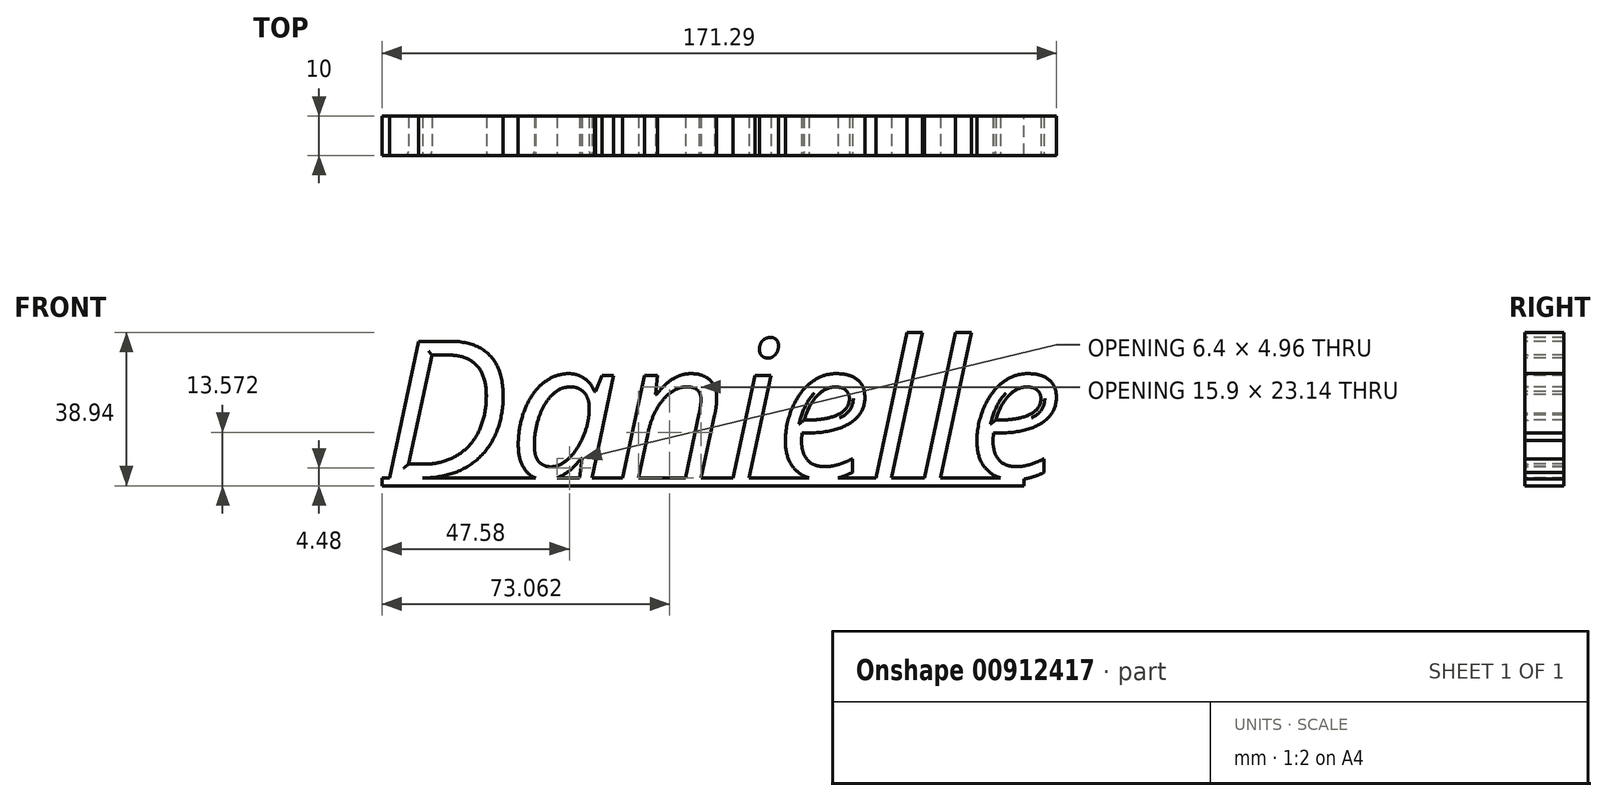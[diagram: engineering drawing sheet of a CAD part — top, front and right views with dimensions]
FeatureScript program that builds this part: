
annotation { "Feature Type Name" : "Feature", "Feature Type Description" : "" }
export const myFeature = defineFeature(function(context is Context, id is Id, definition is map)
    precondition{}
    {
        {
            var Q0;
            Q0=qCreatedBy(makeId("Front.planeOp"),FACE);
            var sketch = newSketch(context, id + "F0", { "sketchPlane" : qUnion([Q0])});
            skText(sketch, "E0", { "text": "Danielle", "fontName": "OpenSans-Italic.ttf"});
            const initialGuessF0  = {"E0": [-0.072, 0, 1, 0, 0.035]};
            skSetInitialGuess(sketch, initialGuessF0);
            skSolve(sketch);
        }
        {
            var Q0;
            Q0 = qSketchRegion(id + "F0", true);
            extrude(context, id + "F1", {"entities" : qUnion([Q0]), "oppositeDirection" : true, "depth" : 10 * mm, "offsetDistance" : 25 * mm});
        }
        {
            var Q0;
            Q0=makeQuery(id+"F1.opExtrude","CAP_FACE",FACE,{"disambiguationData":[OSD([sQuery(id+"F0.wireOp",EDGE,"E0.sketch_text.stroke-16"),sQuery(id+"F0.wireOp",EDGE,"E0.sketch_text.stroke-17"),sQuery(id+"F0.wireOp",EDGE,"E0.sketch_text.stroke-18"),sQuery(id+"F0.wireOp",EDGE,"E0.sketch_text.stroke-19"),sQuery(id+"F0.wireOp",EDGE,"E0.sketch_text.stroke-20"),sQuery(id+"F0.wireOp",EDGE,"E0.sketch_text.stroke-21"),sQuery(id+"F0.wireOp",EDGE,"E0.sketch_text.stroke-22"),sQuery(id+"F0.wireOp",EDGE,"E0.sketch_text.stroke-23"),sQuery(id+"F0.wireOp",EDGE,"E0.sketch_text.stroke-24"),sQuery(id+"F0.wireOp",EDGE,"E0.sketch_text.stroke-25"),sQuery(id+"F0.wireOp",EDGE,"E0.sketch_text.stroke-26"),sQuery(id+"F0.wireOp",EDGE,"E0.sketch_text.stroke-27"),sQuery(id+"F0.wireOp",EDGE,"E0.sketch_text.stroke-28"),sQuery(id+"F0.wireOp",EDGE,"E0.sketch_text.stroke-29"),sQuery(id+"F0.wireOp",EDGE,"E0.sketch_text.stroke-30"),sQuery(id+"F0.wireOp",EDGE,"E0.sketch_text.stroke-31"),sQuery(id+"F0.wireOp",EDGE,"E0.sketch_text.stroke-32"),sQuery(id+"F0.wireOp",EDGE,"E0.sketch_text.stroke-33"),sQuery(id+"F0.wireOp",EDGE,"E0.sketch_text.stroke-34"),sQuery(id+"F0.wireOp",EDGE,"E0.sketch_text.stroke-35"),sQuery(id+"F0.wireOp",EDGE,"E0.sketch_text.stroke-36"),sQuery(id+"F0.wireOp",EDGE,"E0.sketch_text.stroke-37"),sQuery(id+"F0.wireOp",EDGE,"E0.sketch_text.stroke-38"),sQuery(id+"F0.wireOp",EDGE,"E0.sketch_text.stroke-39"),sQuery(id+"F0.wireOp",EDGE,"E0.sketch_text.stroke-40")])],"isStart":true});
            var sketch = newSketch(context, id + "F2", { "sketchPlane" : qUnion([Q0])});
            skLineSegment(sketch, "E1.bottom", {"start": v(-71.88, 0) * mm, "end": v(91.12, 0) * mm});
            skLineSegment(sketch, "E1.top", {"start": v(-71.88, -2) * mm, "end": v(91.12, -2) * mm});
            skLineSegment(sketch, "E1.left", {"start": v(-71.88, 0) * mm, "end": v(-71.88, -2) * mm});
            skLineSegment(sketch, "E1.right", {"start": v(91.12, 0) * mm, "end": v(91.12, -2) * mm});
            skSolve(sketch);
        }
        {
            var Q0;
            Q0=makeQuery(id+"F2.imprint","IMPRINT",FACE,{"disambiguationData":[TD([[makeQuery(id+"F2.imprint","IMPRINT",EDGE,{"derivedFrom":sQuery(id+"F2.wireOp",EDGE,"E1.top")}),1.0]])]});
            extrude(context, id + "F3", {"entities" : qUnion([Q0]), "operationType" : NewBodyOperationType.ADD, "oppositeDirection" : true, "depth" : 10 * mm, "offsetDistance" : 25 * mm});
        }
        {
            var Q0;
            Q0=makeQuery(id+"F1.opExtrude","CAP_EDGE",EDGE,{"disambiguationData":[OSD([sQuery(id+"F0.wireOp",EDGE,"E0.sketch_text.stroke-10")])],"isStart":true});
            var Q1;
            Q1=makeQuery(id+"F1.opExtrude","CAP_EDGE",EDGE,{"disambiguationData":[OSD([sQuery(id+"F0.wireOp",EDGE,"E0.sketch_text.stroke-38")])],"isStart":true});
            var Q2;
            Q2=makeQuery(id+"F1.opExtrude","CAP_EDGE",EDGE,{"disambiguationData":[OSD([sQuery(id+"F0.wireOp",EDGE,"E0.sketch_text.stroke-14")])],"isStart":true});
            var Q3;
            Q3=makeQuery(id+"F1.opExtrude","CAP_EDGE",EDGE,{"disambiguationData":[OSD([sQuery(id+"F0.wireOp",EDGE,"E0.sketch_text.stroke-93")])],"isStart":true});
            var Q4;
            Q4=makeQuery(id+"F1.opExtrude","CAP_EDGE",EDGE,{"disambiguationData":[OSD([sQuery(id+"F0.wireOp",EDGE,"E0.sketch_text.stroke-126")])],"isStart":true});
            fillet(context, id + "F4", {"entities" : qUnion([Q0, Q1, Q2, Q3, Q4]), "radius" : 1 * mm, "tangentPropagation" : true, "allowEdgeOverflow" : false});
        }
    });
